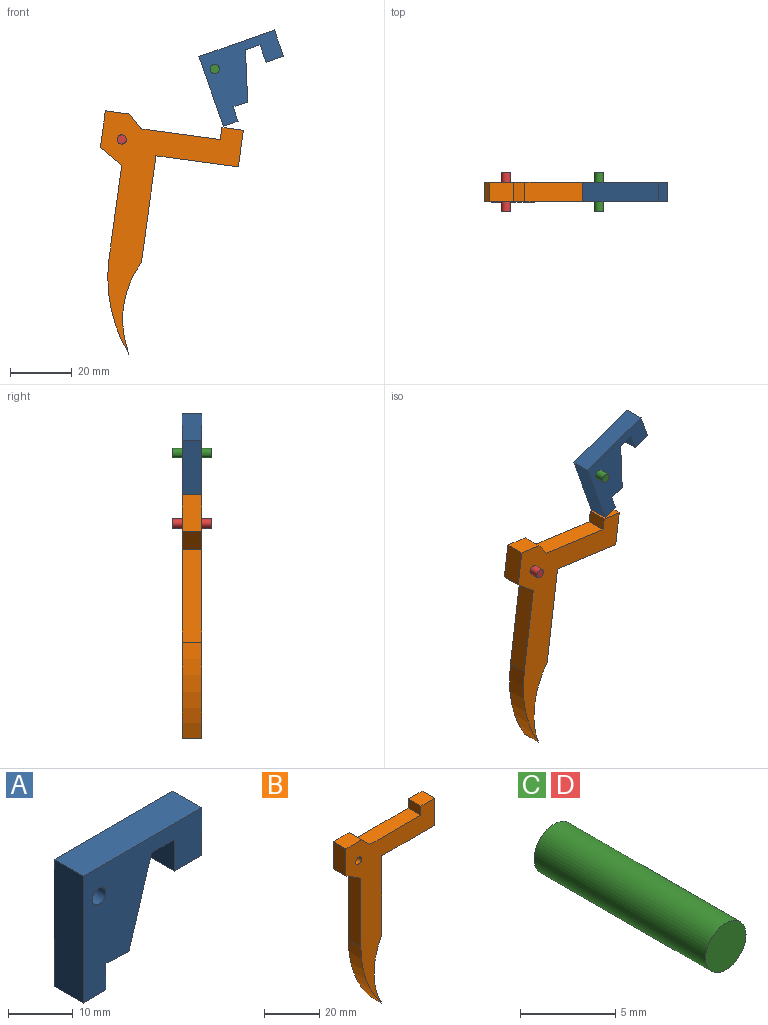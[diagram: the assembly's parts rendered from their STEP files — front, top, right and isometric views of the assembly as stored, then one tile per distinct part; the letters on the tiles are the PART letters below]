
ASSEMBLY  parts=4 mates=2
PART A: 13 faces, bbox 26x6.4x24 mm
  f0: plane 26x6.35mm, normal (0,0,1), area 165.1mm2, adj f1,f9,f11,f12
  f1: plane 24x6.35mm, normal (-1,0,0), area 152.4mm2, adj f0,f2,f11,f12
  f2: plane 6.35x5mm, normal (0,0,-1), area 31.7mm2, adj f1,f3,f11,f12
  f3: plane 6.35x5mm, normal (1,0,0), area 31.7mm2, adj f2,f4,f11,f12
  f4: plane 6.35x5mm, normal (-0.05,0,-1), area 31.8mm2, adj f3,f5,f11,f12
  f5: plane 16.25x6.35mm, normal (0.96,0,-0.29), area 108mm2, adj f4,f6,f11,f12
  f6: plane 6.35x5mm, normal (0,0,-1), area 31.8mm2, adj f5,f7,f11,f12
  f7: plane 6.35x6mm, normal (-1,0,0), area 38.1mm2, adj f6,f8,f11,f12
  f8: plane 6.35x6mm, normal (0,0,-1), area 38.1mm2, adj f7,f9,f11,f12
  f9: plane 9x6.35mm, normal (1,0,0), area 57.1mm2, adj f0,f8,f11,f12
  f10: cylinder r=1.5mm len=6.35mm, axis (0,1,0), area 59.8mm2, adj f11,f12
  f11: plane 26x24mm, normal (0,-1,0), area 333.2mm2, adj f0,f1,f2,f3,f4,f5,f6,f7
  f12: plane 26x24mm, normal (0,1,0), area 333.2mm2, adj f0,f1,f2,f3,f4,f5,f6,f7
PART B: 16 faces, bbox 45.2x6.4x77.2 mm
  f0: plane 7.63x6.35mm, normal (-0.53,0,-0.85), area 57.1mm2, adj f1,f12,f14,f15
  f1: plane 30.47x6.35mm, normal (-1,0,0), area 193.5mm2, adj f0,f2,f14,f15
  f2: cylinder r=47.72mm len=30mm, axis (0,1,0), area 206mm2, adj f1,f3,f14,f15
  f3: cylinder r=31.18mm len=30mm, axis (0,1,0), area 198.7mm2, adj f2,f4,f14,f15
  f4: plane 35x6.35mm, normal (1,0,0), area 222.2mm2, adj f3,f5,f14,f15
  f5: plane 27x6.35mm, normal (0,0,-1), area 171.4mm2, adj f4,f6,f14,f15
  f6: plane 12x6.35mm, normal (1,0,0), area 76.2mm2, adj f5,f7,f14,f15
  f7: plane 7x6.35mm, normal (0,0,1), area 44.4mm2, adj f6,f8,f14,f15
  f8: plane 6.35x4mm, normal (-1,0,0), area 25.4mm2, adj f7,f9,f14,f15
  f9: plane 26x6.35mm, normal (0,0,1), area 165.1mm2, adj f8,f10,f14,f15
  f10: plane 6.35x4.24mm, normal (0.71,0,0.71), area 38.1mm2, adj f9,f11,f14,f15
  f11: plane 8x6.35mm, normal (0,0,1), area 50.8mm2, adj f10,f12,f14,f15
  f12: plane 12x6.35mm, normal (-1,0,0), area 76.2mm2, adj f0,f11,f14,f15
  f13: cylinder r=1.5mm len=6.35mm, axis (0,1,0), area 59.8mm2, adj f14,f15
  f14: plane 77.24x45.24mm, normal (0,-1,0), area 953mm2, adj f0,f1,f2,f3,f4,f5,f6,f7
  f15: plane 77.24x45.24mm, normal (0,1,0), area 953mm2, adj f0,f1,f2,f3,f4,f5,f6,f7
PART C: 3 faces, bbox 3x12.7x3 mm
  f0: cylinder r=1.5mm len=12.7mm, axis (0,1,0), area 119.7mm2, adj f1,f2
  f1: plane 3x3mm, normal (0,-1,0), area 7.1mm2, adj f0
  f2: plane 3x3mm, normal (0,1,0), area 7.1mm2, adj f0
PART D: same geometry as C
PLACE A rot(axis=(0,-1,0),19.5deg) t=(7.01,-12.78,32.86)mm
PLACE B rot(axis=(0,1,0),7.7deg) t=(-20.53,-12.83,-13.16)mm
PLACE C t=(-40.38,-9.6,43.32)mm fixed
PLACE D t=(-70.58,-9.65,20.46)mm fixed
MATE revolute C.f0 <-> A.f10  axis (0,1,0) through (-40.38,-15.95,43.32)mm
MATE revolute D.f0 <-> B.f13  axis (0,1,0) through (-70.58,-16,20.46)mm
